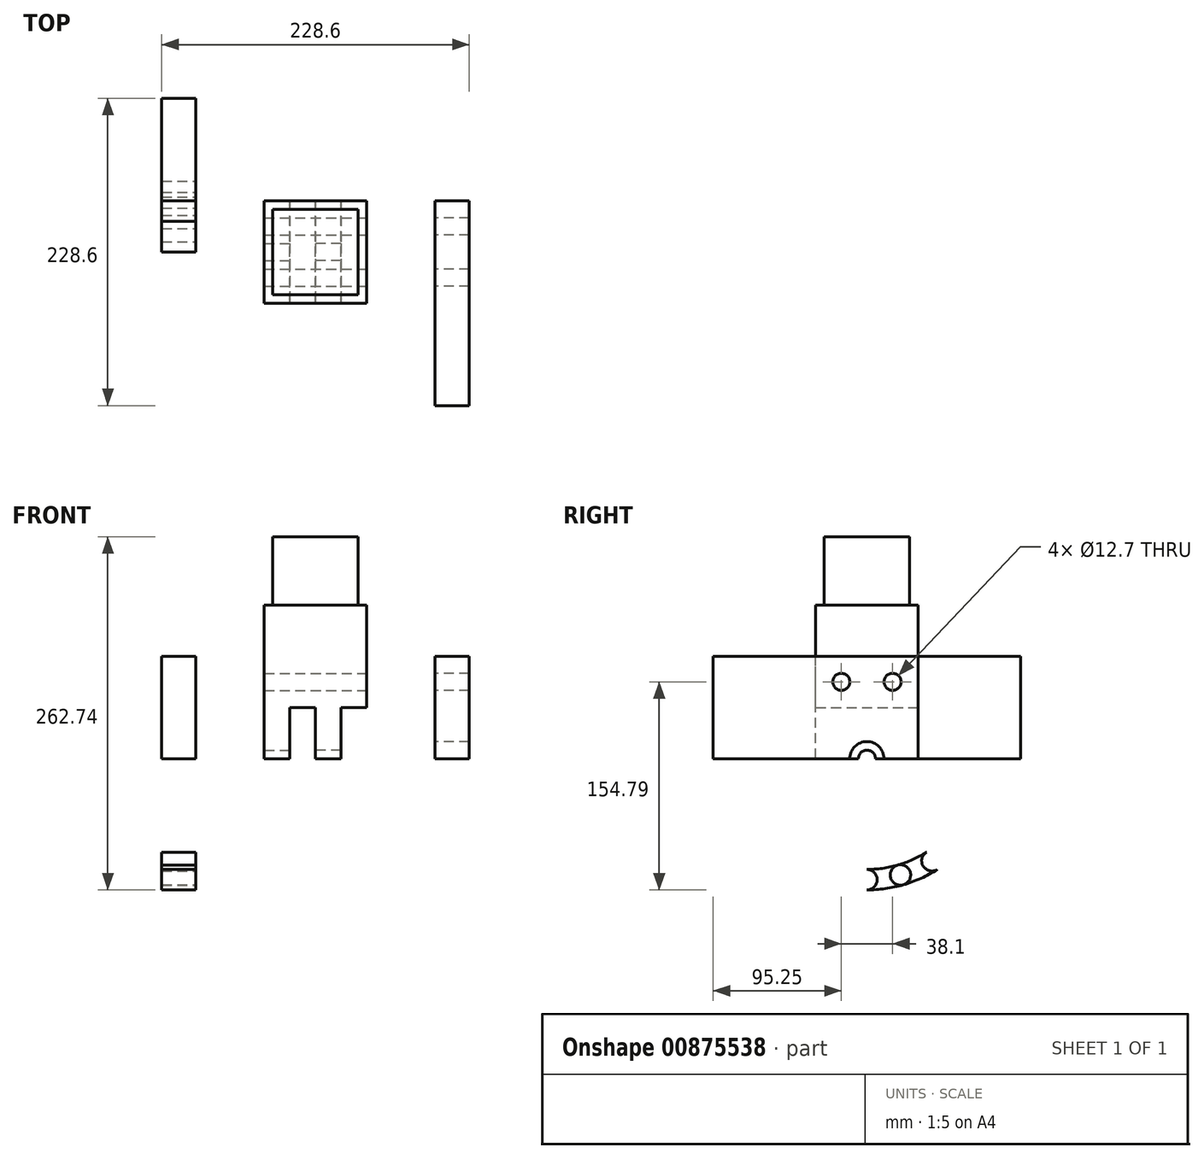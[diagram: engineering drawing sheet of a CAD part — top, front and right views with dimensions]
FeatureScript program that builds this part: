
annotation { "Feature Type Name" : "Feature", "Feature Type Description" : "" }
export const myFeature = defineFeature(function(context is Context, id is Id, definition is map)
    precondition{}
    {
        {
            var Q0;
            Q0=qCreatedBy(makeId("Right.planeOp"),FACE);
            var sketch = newSketch(context, id + "F0", { "sketchPlane" : qUnion([Q0])});
            skLineSegment(sketch, "E0.bottom", {"start": v(38.1, -57.15) * mm, "end": v(-38.1, -57.15) * mm});
            skLineSegment(sketch, "E0.top", {"start": v(38.1, 57.15) * mm, "end": v(-38.1, 57.15) * mm});
            skLineSegment(sketch, "E0.left", {"start": v(38.1, -57.15) * mm, "end": v(38.1, 57.15) * mm});
            skLineSegment(sketch, "E0.right", {"start": v(-38.1, -57.15) * mm, "end": v(-38.1, 57.15) * mm});
            skPoint(sketch, "E0.middle", {"position": v(0, 0) * mm});
            skArc(sketch, "E1", {"start": v(38.1, -57.15) * mm, "mid": v(0, -95.25) * mm, "end": v(-38.1, -57.15) * mm});
            skCircle(sketch, "E2", {"center": v(0, -57.15) * mm, "radius": 6.35 * mm});
            skLineSegment(sketch, "E3", {"start": v(-38.1, -19.05) * mm, "end": v(38.1, -19.05) * mm});
            skSolve(sketch);
        }
        {
            var Q0;
            {var subQ0=sQuery(id+"F0.wireOp",EDGE,"E0.top");Q0=makeQuery(id+"F0.imprint","IMPRINT",FACE,{"disambiguationData":[TD([[makeQuery(id+"F0.imprint","IMPRINT",EDGE,{"derivedFrom":subQ0}),1.0]])]});}
            extrude(context, id + "F1", {"entities" : qUnion([Q0]), "endBound" : BoundingType.SYMMETRIC, "depth" : 76.2 * mm, "offsetDistance" : 25.4 * mm});
        }
        {
            var Q0;
            {var subQ4=sQuery(id+"F0.wireOp",EDGE,"E3");Q0=makeQuery(id+"F0.imprint","IMPRINT",FACE,{"disambiguationData":[TD([[makeQuery(id+"F0.imprint","IMPRINT",EDGE,{"derivedFrom":subQ4}),-1.0]])]});}
            var Q1;
            {var subQ0=sQuery(id+"F0.wireOp",EDGE,"E1");Q1=makeQuery(id+"F0.imprint","IMPRINT",FACE,{"disambiguationData":[TD([[makeQuery(id+"F0.imprint","IMPRINT",EDGE,{"derivedFrom":subQ0}),-1.0]])]});}
            extrude(context, id + "F2", {"entities" : qUnion([Q0, Q1]), "operationType" : NewBodyOperationType.ADD, "depth" : 19.05 * mm, "offsetDistance" : 25.4 * mm});
        }
        {
            var Q0;
            {var subQ4=sQuery(id+"F0.wireOp",EDGE,"E3");Q0=makeQuery(id+"F0.imprint","IMPRINT",FACE,{"disambiguationData":[TD([[makeQuery(id+"F0.imprint","IMPRINT",EDGE,{"derivedFrom":subQ4}),-1.0]])]});}
            var Q1;
            {var subQ0=sQuery(id+"F0.wireOp",EDGE,"E1");Q1=makeQuery(id+"F0.imprint","IMPRINT",FACE,{"disambiguationData":[TD([[makeQuery(id+"F0.imprint","IMPRINT",EDGE,{"derivedFrom":subQ0}),-1.0]])]});}
            extrude(context, id + "F3", {"entities" : qUnion([Q0, Q1]), "operationType" : NewBodyOperationType.ADD, "oppositeDirection" : true, "depth" : 38.1 * mm, "offsetDistance" : 25.4 * mm, "hasSecondDirection" : true, "secondDirectionOppositeDirection" : true, "secondDirectionDepth" : 19.05 * mm});
        }
        {
            var Q0;
            Q0=makeQuery(id+"F1.opExtrude","SWEPT_FACE",FACE,{"disambiguationData":[OSD([sQuery(id+"F0.wireOp",EDGE,"E0.top")])]});
            var sketch = newSketch(context, id + "F4", { "sketchPlane" : qUnion([Q0])});
            skLineSegment(sketch, "E4.bottom", {"start": v(31.75, -31.75) * mm, "end": v(-31.75, -31.75) * mm});
            skLineSegment(sketch, "E4.top", {"start": v(31.75, 31.75) * mm, "end": v(-31.75, 31.75) * mm});
            skLineSegment(sketch, "E4.left", {"start": v(31.75, -31.75) * mm, "end": v(31.75, 31.75) * mm});
            skLineSegment(sketch, "E4.right", {"start": v(-31.75, -31.75) * mm, "end": v(-31.75, 31.75) * mm});
            skPoint(sketch, "E4.middle", {"position": v(0, 0) * mm});
            skSolve(sketch);
        }
        {
            var Q0;
            Q0=makeQuery(id+"F4.imprint","IMPRINT",FACE,{"disambiguationData":[TD([[makeQuery(id+"F4.imprint","IMPRINT",EDGE,{"derivedFrom":sQuery(id+"F4.wireOp",EDGE,"E4.bottom")}),-1.0]])]});
            extrude(context, id + "F5", {"entities" : qUnion([Q0]), "operationType" : NewBodyOperationType.ADD, "depth" : 50.8 * mm, "offsetDistance" : 25.4 * mm});
        }
        {
            var Q0;
            Q0=makeQuery(id+"F1.opExtrude","CAP_FACE",FACE,{"disambiguationData":[OSD([sQuery(id+"F0.wireOp",EDGE,"E0.top"),sQuery(id+"F0.wireOp",EDGE,"E0.left"),sQuery(id+"F0.wireOp",EDGE,"E0.right"),sQuery(id+"F0.wireOp",EDGE,"E3")])],"isStart":false});
            var sketch = newSketch(context, id + "F6", { "sketchPlane" : qUnion([Q0])});
            skLineSegment(sketch, "E5", {"start": v(38.1, 19.05) * mm, "end": v(-114.3, 19.05) * mm});
            skLineSegment(sketch, "E6", {"start": v(38.1, 19.05) * mm, "end": v(38.1, -164.91) * mm});
            skArc(sketch, "E7", {"start": v(38.1, -164.91) * mm, "mid": v(-66, -150.48) * mm, "end": v(-114.3, -57.15) * mm});
            skLineSegment(sketch, "E8", {"start": v(-114.3, 19.05) * mm, "end": v(-114.3, -57.15) * mm});
            skCircle(sketch, "E9", {"center": v(0, -147.17) * mm, "radius": 7.62 * mm});
            skArc(sketch, "E10", {"start": v(0, -147.17) * mm, "mid": v(-48.34, -133.09) * mm, "end": v(-81.56, -95.25) * mm});
            skLineSegment(sketch, "E11", {"start": v(-114.3, -57.15) * mm, "end": v(38.1, -57.15) * mm});
            skCircle(sketch, "E12", {"center": v(-81.56, -95.25) * mm, "radius": 7.62 * mm});
            skArc(sketch, "E13", {"start": v(0, -154.8) * mm, "mid": v(-52.43, -139.52) * mm, "end": v(-88.46, -98.48) * mm});
            skArc(sketch, "E14", {"start": v(0, -139.55) * mm, "mid": v(-44.25, -126.66) * mm, "end": v(-74.66, -92.02) * mm});
            skCircle(sketch, "E15", {"center": v(19.05, 0) * mm, "radius": 6.35 * mm});
            skCircle(sketch, "E16", {"center": v(-19.05, 0) * mm, "radius": 6.35 * mm});
            skCircle(sketch, "E17", {"center": v(0, -57.15) * mm, "radius": 12.7 * mm});
            skSolve(sketch);
        }
        {
            var Q0;
            {var subQ3=sQuery(id+"F6.wireOp",EDGE,"E8");Q0=makeQuery(id+"F6.imprint","IMPRINT",FACE,{"disambiguationData":[TD([[makeQuery(id+"F6.imprint","IMPRINT",EDGE,{"derivedFrom":subQ3}),1.0]])]});}
            var Q1;
            {var subQ5=makeQuery(id+"F1.opExtrude","CAP_EDGE",EDGE,{"disambiguationData":[OSD([sQuery(id+"F0.wireOp",EDGE,"E3")])],"isStart":false});Q1=makeQuery(id+"F6.imprint","IMPRINT",FACE,{"disambiguationData":[TD([[makeQuery(id+"F6.imprint","IMPRINT",EDGE,{"derivedFrom":subQ5}),1.0]])]});}
            var Q2;
            {var subQ1=sQuery(id+"F6.wireOp",EDGE,"E7");Q2=makeQuery(id+"F6.imprint","IMPRINT",FACE,{"disambiguationData":[TD([[makeQuery(id+"F6.imprint","IMPRINT",EDGE,{"derivedFrom":subQ1}),-1.0]])]});}
            extrude(context, id + "F7", {"entities" : qUnion([Q0, Q1, Q2]), "depth" : 76.2 * mm, "offsetDistance" : 25.4 * mm, "hasSecondDirection" : true, "secondDirectionOppositeDirection" : false, "secondDirectionDepth" : 50.8 * mm});
        }
        {
            var Q0;
            Q0=makeQuery(id+"F6.imprint","IMPRINT",FACE,{"disambiguationData":[TD([[makeQuery(id+"F6.imprint","IMPRINT",EDGE,{"derivedFrom":sQuery(id+"F6.wireOp",EDGE,"E15")}),1.0]])]});
            var Q1;
            Q1=makeQuery(id+"F6.imprint","IMPRINT",FACE,{"disambiguationData":[TD([[makeQuery(id+"F6.imprint","IMPRINT",EDGE,{"derivedFrom":sQuery(id+"F6.wireOp",EDGE,"E16")}),1.0]])]});
            extrude(context, id + "F8", {"entities" : qUnion([Q0, Q1]), "operationType" : NewBodyOperationType.REMOVE, "oppositeDirection" : true, "depth" : 76.2 * mm, "offsetDistance" : 25.4 * mm});
        }
        {
            var Q0;
            {var subQ0=sQuery(id+"F0.wireOp",EDGE,"E3");var subQ1=sQuery(id+"F0.wireOp",EDGE,"E0.right");var subQ2=sQuery(id+"F0.wireOp",EDGE,"E0.left");Q0=makeQuery(id+"F3.boolean.opBoolean","MERGE",FACE,{"derivedFrom":[makeQuery(id+"F1.opExtrude","CAP_FACE",FACE,{"disambiguationData":[OSD([sQuery(id+"F0.wireOp",EDGE,"E0.top"),subQ2,subQ1,subQ0])],"isStart":true}),makeQuery(id+"F3.opExtrude","CAP_FACE",FACE,{"disambiguationData":[OSD([subQ2,subQ1,sQuery(id+"F0.wireOp",EDGE,"E1"),sQuery(id+"F0.wireOp",EDGE,"E2"),subQ0])],"isStart":false})]});}
            var sketch = newSketch(context, id + "F9", { "sketchPlane" : qUnion([Q0])});
            skLineSegment(sketch, "E18", {"start": v(38.1, 19.05) * mm, "end": v(-114.3, 19.05) * mm});
            skLineSegment(sketch, "E19", {"start": v(38.1, 19.05) * mm, "end": v(38.1, -164.91) * mm});
            skArc(sketch, "E20", {"start": v(38.1, -164.91) * mm, "mid": v(-66, -150.48) * mm, "end": v(-114.3, -57.15) * mm});
            skLineSegment(sketch, "E21", {"start": v(-114.3, 19.05) * mm, "end": v(-114.3, -57.15) * mm});
            skCircle(sketch, "E22", {"center": v(0, -147.17) * mm, "radius": 7.62 * mm});
            skArc(sketch, "E23", {"start": v(0, -147.17) * mm, "mid": v(-48.34, -133.09) * mm, "end": v(-81.56, -95.25) * mm});
            skLineSegment(sketch, "E24", {"start": v(-114.3, -57.15) * mm, "end": v(38.1, -57.15) * mm});
            skCircle(sketch, "E25", {"center": v(-81.56, -95.25) * mm, "radius": 7.62 * mm});
            skArc(sketch, "E26", {"start": v(0, -154.8) * mm, "mid": v(-52.43, -139.52) * mm, "end": v(-88.46, -98.48) * mm});
            skArc(sketch, "E27", {"start": v(0, -139.55) * mm, "mid": v(-44.25, -126.66) * mm, "end": v(-74.66, -92.02) * mm});
            skCircle(sketch, "E28", {"center": v(51.95, 73.37) * mm, "radius": 6.35 * mm});
            skCircle(sketch, "E29", {"center": v(13.85, 73.37) * mm, "radius": 6.35 * mm});
            skCircle(sketch, "E30", {"center": v(0, -57.15) * mm, "radius": 12.7 * mm});
            skCircle(sketch, "E31", {"center": v(-48.34, -133.09) * mm, "radius": 7.62 * mm});
            skCircle(sketch, "E32", {"center": v(-24.93, -143.65) * mm, "radius": 7.62 * mm});
            skCircle(sketch, "E33", {"center": v(-70.19, -113.52) * mm, "radius": 7.62 * mm});
            skSolve(sketch);
        }
        {
            var Q0;
            {var subQ16=sQuery(id+"F9.wireOp",EDGE,"E20");Q0=makeQuery(id+"F9.imprint","IMPRINT",FACE,{"disambiguationData":[TD([[makeQuery(id+"F9.imprint","IMPRINT",EDGE,{"derivedFrom":subQ16}),-1.0]])]});}
            var Q1;
            {var subQ0=sQuery(id+"F9.wireOp",EDGE,"E25");var subQ1=sQuery(id+"F9.wireOp",EDGE,"E23");var subQ2=makeQuery(id+"F9.imprint","INTERSECT",VERTEX,{"derivedFrom":[subQ1,subQ0]});Q1=makeQuery(id+"F9.imprint","IMPRINT",FACE,{"disambiguationData":[TD([[makeQuery(id+"F9.imprint","IMPRINT",EDGE,{"disambiguationData":[TD([[subQ2,1.0]])],"derivedFrom":subQ1}),1.0]])]});}
            var Q2;
            {var subQ0=sQuery(id+"F9.wireOp",EDGE,"E25");var subQ1=sQuery(id+"F9.wireOp",EDGE,"E23");var subQ2=makeQuery(id+"F9.imprint","INTERSECT",VERTEX,{"derivedFrom":[subQ1,subQ0]});Q2=makeQuery(id+"F9.imprint","IMPRINT",FACE,{"disambiguationData":[TD([[makeQuery(id+"F9.imprint","IMPRINT",EDGE,{"disambiguationData":[TD([[subQ2,1.0]])],"derivedFrom":subQ1}),-1.0]])]});}
            var Q3;
            {var subQ0=sQuery(id+"F9.wireOp",EDGE,"E31");var subQ1=sQuery(id+"F9.wireOp",EDGE,"E23");var subQ2=makeQuery(id+"F9.imprint","INTERSECT",VERTEX,{"disambiguationData":[OD(1.0)],"derivedFrom":[subQ1,subQ0]});Q3=makeQuery(id+"F9.imprint","IMPRINT",FACE,{"disambiguationData":[TD([[makeQuery(id+"F9.imprint","IMPRINT",EDGE,{"disambiguationData":[TD([[subQ2,-1.0]])],"derivedFrom":subQ1}),1.0]])]});}
            var Q4;
            {var subQ0=sQuery(id+"F9.wireOp",EDGE,"E31");var subQ1=sQuery(id+"F9.wireOp",EDGE,"E23");var subQ2=makeQuery(id+"F9.imprint","INTERSECT",VERTEX,{"disambiguationData":[OD(1.0)],"derivedFrom":[subQ1,subQ0]});Q4=makeQuery(id+"F9.imprint","IMPRINT",FACE,{"disambiguationData":[TD([[makeQuery(id+"F9.imprint","IMPRINT",EDGE,{"disambiguationData":[TD([[subQ2,-1.0]])],"derivedFrom":subQ1}),-1.0]])]});}
            var Q5;
            {var subQ0=sQuery(id+"F9.wireOp",EDGE,"E32");var subQ1=sQuery(id+"F9.wireOp",EDGE,"E23");var subQ2=makeQuery(id+"F9.imprint","INTERSECT",VERTEX,{"disambiguationData":[OD(1.0)],"derivedFrom":[subQ1,subQ0]});Q5=makeQuery(id+"F9.imprint","IMPRINT",FACE,{"disambiguationData":[TD([[makeQuery(id+"F9.imprint","IMPRINT",EDGE,{"disambiguationData":[TD([[subQ2,-1.0]])],"derivedFrom":subQ1}),1.0]])]});}
            var Q6;
            {var subQ0=sQuery(id+"F9.wireOp",EDGE,"E32");var subQ1=sQuery(id+"F9.wireOp",EDGE,"E23");var subQ2=makeQuery(id+"F9.imprint","INTERSECT",VERTEX,{"disambiguationData":[OD(1.0)],"derivedFrom":[subQ1,subQ0]});Q6=makeQuery(id+"F9.imprint","IMPRINT",FACE,{"disambiguationData":[TD([[makeQuery(id+"F9.imprint","IMPRINT",EDGE,{"disambiguationData":[TD([[subQ2,-1.0]])],"derivedFrom":subQ1}),-1.0]])]});}
            var Q7;
            {var subQ0=sQuery(id+"F9.wireOp",EDGE,"E26");var subQ1=sQuery(id+"F9.wireOp",EDGE,"E22");var subQ2=makeQuery(id+"F9.imprint","INTERSECT",VERTEX,{"derivedFrom":[subQ1,subQ0]});Q7=makeQuery(id+"F9.imprint","IMPRINT",FACE,{"disambiguationData":[TD([[makeQuery(id+"F9.imprint","IMPRINT",EDGE,{"disambiguationData":[TD([[subQ2,1.0]])],"derivedFrom":subQ1}),-1.0]])]});}
            var Q8;
            {var subQ0=sQuery(id+"F9.wireOp",EDGE,"E27");var subQ1=sQuery(id+"F9.wireOp",EDGE,"E22");var subQ2=makeQuery(id+"F9.imprint","INTERSECT",VERTEX,{"derivedFrom":[subQ1,subQ0]});Q8=makeQuery(id+"F9.imprint","IMPRINT",FACE,{"disambiguationData":[TD([[makeQuery(id+"F9.imprint","IMPRINT",EDGE,{"disambiguationData":[TD([[subQ2,-1.0]])],"derivedFrom":subQ1}),-1.0]])]});}
            var Q9;
            {var subQ2=makeQuery(id+"F3.opExtrude","CAP_EDGE",EDGE,{"disambiguationData":[OSD([sQuery(id+"F0.wireOp",EDGE,"E1")])],"isStart":false});Q9=makeQuery(id+"F9.imprint","IMPRINT",FACE,{"disambiguationData":[TD([[makeQuery(id+"F9.imprint","IMPRINT",EDGE,{"derivedFrom":subQ2}),1.0]])]});}
            var Q10;
            {var subQ0=sQuery(id+"F9.wireOp",EDGE,"E21");Q10=makeQuery(id+"F9.imprint","IMPRINT",FACE,{"disambiguationData":[TD([[makeQuery(id+"F9.imprint","IMPRINT",EDGE,{"derivedFrom":subQ0}),1.0]])]});}
            var Q11;
            Q11=makeQuery(id+"F9.imprint","IMPRINT",FACE,{"disambiguationData":[TD([[makeQuery(id+"F9.imprint","IMPRINT",EDGE,{"derivedFrom":makeQuery(id+"F8.boolean.opBoolean","COPY",EDGE,{"derivedFrom":makeQuery(id+"F8.opExtrude","CAP_EDGE",EDGE,{"disambiguationData":[OSD([sQuery(id+"F6.wireOp",EDGE,"E15")])],"isStart":false})})}),1.0]])]});
            extrude(context, id + "F10", {"entities" : qUnion([Q0, Q1, Q2, Q3, Q4, Q5, Q6, Q7, Q8, Q9, Q10, Q11]), "operationType" : NewBodyOperationType.ADD, "depth" : 76.2 * mm, "offsetDistance" : 25.4 * mm, "hasSecondDirection" : true, "secondDirectionOppositeDirection" : false, "secondDirectionDepth" : 50.8 * mm});
        }
    });
